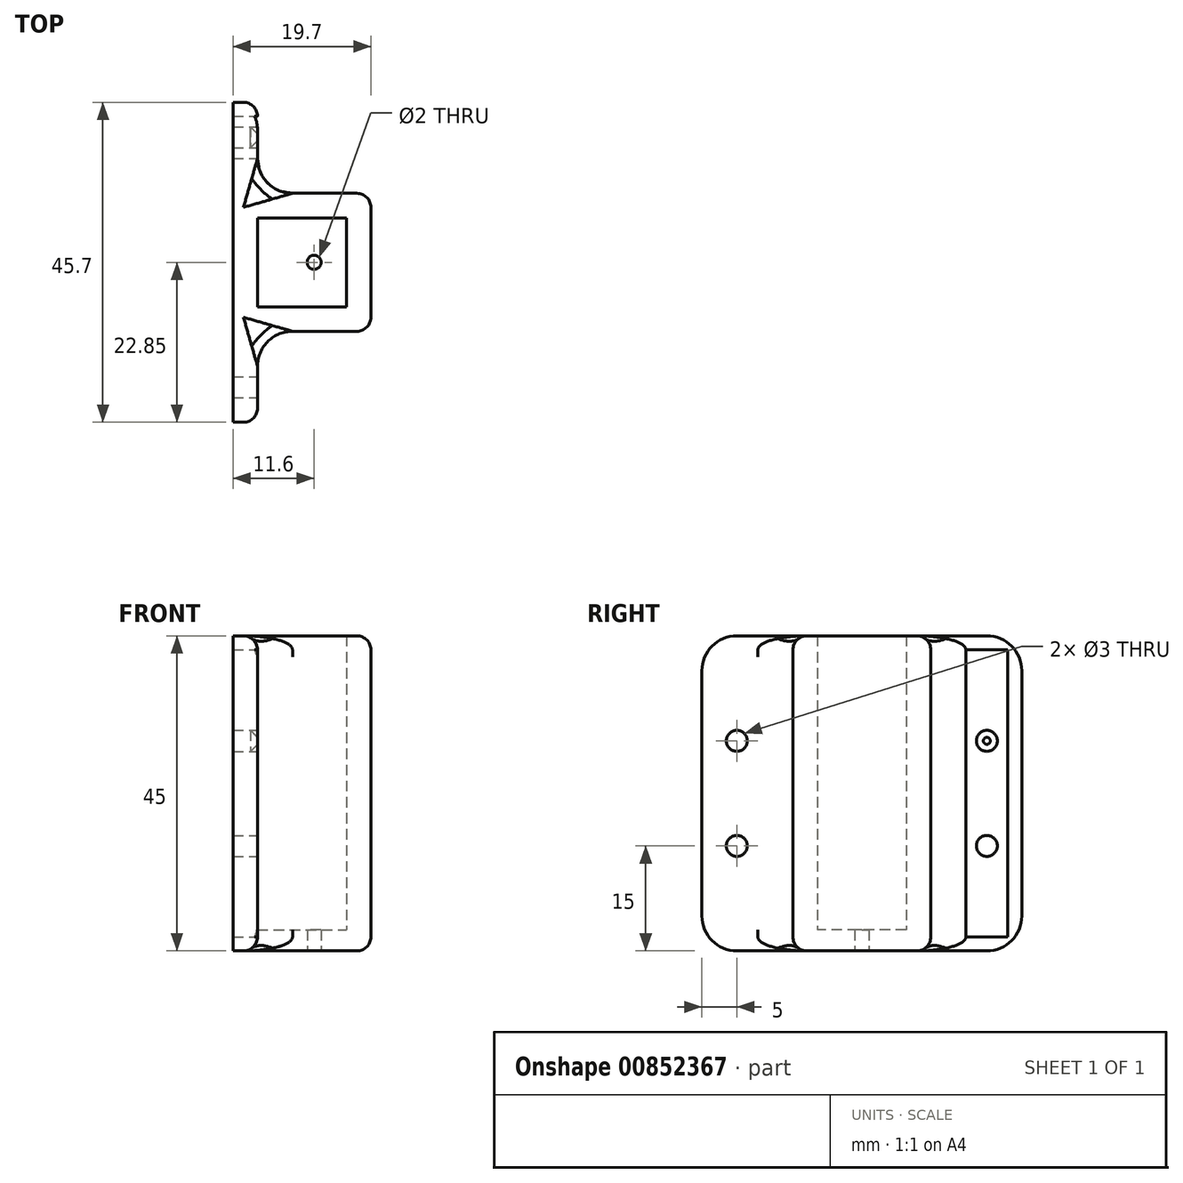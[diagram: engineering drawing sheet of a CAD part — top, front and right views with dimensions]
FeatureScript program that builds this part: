
annotation { "Feature Type Name" : "Feature", "Feature Type Description" : "" }
export const myFeature = defineFeature(function(context is Context, id is Id, definition is map)
    precondition{}
    {
        {
            var Q0;
            Q0=qCreatedBy(makeId("Top.planeOp"),FACE);
            var sketch = newSketch(context, id + "F0", { "sketchPlane" : qUnion([Q0])});
            skLineSegment(sketch, "E0.bottom", {"start": v(0, 6.35) * mm, "end": v(12.7, 6.35) * mm});
            skLineSegment(sketch, "E0.top", {"start": v(0, -6.35) * mm, "end": v(12.7, -6.35) * mm});
            skLineSegment(sketch, "E0.left", {"start": v(0, 6.35) * mm, "end": v(0, -6.35) * mm});
            skLineSegment(sketch, "E0.right", {"start": v(12.7, 6.35) * mm, "end": v(12.7, -6.35) * mm});
            skLineSegment(sketch, "E1.0", {"start": v(0, 9.85) * mm, "end": v(16.2, 9.85) * mm});
            skLineSegment(sketch, "E1.1", {"start": v(-3.5, 9.85) * mm, "end": v(-3.5, -9.85) * mm});
            skLineSegment(sketch, "E1.2", {"start": v(0, -9.85) * mm, "end": v(16.2, -9.85) * mm});
            skLineSegment(sketch, "E1.3", {"start": v(16.2, 9.85) * mm, "end": v(16.2, -9.85) * mm});
            skLineSegment(sketch, "E2.top", {"start": v(-3.5, 22.85) * mm, "end": v(0, 22.85) * mm});
            skLineSegment(sketch, "E2.left", {"start": v(-3.5, -9.85) * mm, "end": v(-3.5, 22.85) * mm});
            skLineSegment(sketch, "E3.trimOffspring", {"start": v(0, -6.35) * mm, "end": v(0, 6.35) * mm});
            skPoint(sketch, "E2.bottom.start.orphan", {"position": v(-3.5, -21.69) * mm});
            skLineSegment(sketch, "E4.trimOffspring", {"start": v(0, 9.85) * mm, "end": v(0, 22.85) * mm});
            skLineSegment(sketch, "E5.MirrorCS", {"start": v(0, -9.85) * mm, "end": v(0, -22.85) * mm});
            skLineSegment(sketch, "E6.MirrorCS", {"start": v(-3.5, -22.85) * mm, "end": v(0, -22.85) * mm});
            skLineSegment(sketch, "E7.MirrorCS", {"start": v(-3.5, 9.85) * mm, "end": v(-3.5, -22.85) * mm});
            skSolve(sketch);
        }
        {
            var Q0;
            Q0=qSketchRegion(id+"F0",true);
            extrude(context, id + "F1", {"entities" : qUnion([Q0]), "depth" : 45 * mm, "offsetDistance" : 25 * mm});
        }
        {
            var Q0;
            Q0=makeQuery(id+"F0.imprint","IMPRINT",FACE,{"disambiguationData":[TD([[makeQuery(id+"F0.imprint","IMPRINT",EDGE,{"derivedFrom":sQuery(id+"F0.wireOp",EDGE,"E0.bottom")}),-1.0]])]});
            extrude(context, id + "F2", {"entities" : qUnion([Q0]), "operationType" : NewBodyOperationType.ADD, "depth" : 3 * mm, "offsetDistance" : 25 * mm});
        }
        {
            var Q0;
            {var subQ0=sQuery(id+"F0.wireOp",EDGE,"E3.trimOffspring");var subQ1=sQuery(id+"F0.wireOp",EDGE,"E0.right");var subQ2=sQuery(id+"F0.wireOp",EDGE,"E0.top");var subQ3=sQuery(id+"F0.wireOp",EDGE,"E0.bottom");Q0=makeQuery(id+"F2.boolean.opBoolean","MERGE",FACE,{"derivedFrom":[makeQuery(id+"F1.opExtrude","CAP_FACE",FACE,{"disambiguationData":[OSD([subQ3,subQ2,subQ1,sQuery(id+"F0.wireOp",EDGE,"E1.0"),sQuery(id+"F0.wireOp",EDGE,"E1.2"),sQuery(id+"F0.wireOp",EDGE,"E1.3"),sQuery(id+"F0.wireOp",EDGE,"E2.top"),sQuery(id+"F0.wireOp",EDGE,"E2.left"),subQ0,sQuery(id+"F0.wireOp",EDGE,"E4.trimOffspring"),sQuery(id+"F0.wireOp",EDGE,"E5.MirrorCS"),sQuery(id+"F0.wireOp",EDGE,"E6.MirrorCS"),sQuery(id+"F0.wireOp",EDGE,"E7.MirrorCS")])],"isStart":true}),makeQuery(id+"F2.opExtrude","CAP_FACE",FACE,{"disambiguationData":[OSD([subQ3,subQ2,subQ1,subQ0])],"isStart":true})]});}
            var sketch = newSketch(context, id + "F3", { "sketchPlane" : qUnion([Q0])});
            skLineSegment(sketch, "E8", {"start": v(0, 0) * mm, "end": v(16.2, 0) * mm, "construction": true});
            skCircle(sketch, "E9", {"center": v(8.1, 0) * mm, "radius": 1 * mm});
            skSolve(sketch);
        }
        {
            var Q0;
            Q0=makeQuery(id+"F3.imprint","IMPRINT",FACE,{"disambiguationData":[TD([[makeQuery(id+"F3.imprint","IMPRINT",EDGE,{"derivedFrom":sQuery(id+"F3.wireOp",EDGE,"E9")}),1.0]])]});
            extrude(context, id + "F4", {"entities" : qUnion([Q0]), "operationType" : NewBodyOperationType.REMOVE, "endBound" : BoundingType.THROUGH_ALL, "oppositeDirection" : true, "depth" : 25 * mm, "offsetDistance" : 25 * mm});
        }
        {
            var Q0;
            Q0=makeQuery(id+"F1.opExtrude","CAP_EDGE",EDGE,{"disambiguationData":[OSD([sQuery(id+"F0.wireOp",EDGE,"E6.MirrorCS")])],"isStart":false});
            var Q1;
            Q1=makeQuery(id+"F1.opExtrude","CAP_EDGE",EDGE,{"disambiguationData":[OSD([sQuery(id+"F0.wireOp",EDGE,"E2.top")])],"isStart":false});
            var Q2;
            Q2=makeQuery(id+"F1.opExtrude","CAP_EDGE",EDGE,{"disambiguationData":[OSD([sQuery(id+"F0.wireOp",EDGE,"E6.MirrorCS")])],"isStart":true});
            var Q3;
            Q3=makeQuery(id+"F1.opExtrude","CAP_EDGE",EDGE,{"disambiguationData":[OSD([sQuery(id+"F0.wireOp",EDGE,"E2.top")])],"isStart":true});
            fillet(context, id + "F5", {"entities" : qUnion([Q0, Q1, Q2, Q3]), "radius" : 5 * mm, "tangentPropagation" : true, "allowEdgeOverflow" : false});
        }
        {
            var Q0;
            Q0=makeQuery(id+"F1.opExtrude","CAP_EDGE",EDGE,{"disambiguationData":[OSD([sQuery(id+"F0.wireOp",EDGE,"E1.3")])],"isStart":false});
            var Q1;
            Q1=makeQuery(id+"F1.opExtrude","CAP_EDGE",EDGE,{"disambiguationData":[OSD([sQuery(id+"F0.wireOp",EDGE,"E1.2")])],"isStart":false});
            var Q2;
            Q2=makeQuery(id+"F1.opExtrude","CAP_EDGE",EDGE,{"disambiguationData":[OSD([sQuery(id+"F0.wireOp",EDGE,"E1.0")])],"isStart":false});
            var Q3;
            Q3=makeQuery(id+"F1.opExtrude","CAP_EDGE",EDGE,{"disambiguationData":[OSD([sQuery(id+"F0.wireOp",EDGE,"E4.trimOffspring")])],"isStart":false});
            var Q4;
            Q4=makeQuery(id+"F1.opExtrude","CAP_EDGE",EDGE,{"disambiguationData":[OSD([sQuery(id+"F0.wireOp",EDGE,"E5.MirrorCS")])],"isStart":false});
            var Q5;
            Q5=makeQuery(id+"F1.opExtrude","SWEPT_EDGE",EDGE,{"disambiguationData":[OSD([sQuery(id+"F0.wireOp",EDGE,"E5.MirrorCS"),sQuery(id+"F0.wireOp",EDGE,"E6.MirrorCS")])]});
            var Q6;
            Q6=makeQuery(id+"F1.opExtrude","SWEPT_EDGE",EDGE,{"disambiguationData":[OSD([sQuery(id+"F0.wireOp",EDGE,"E2.top"),sQuery(id+"F0.wireOp",EDGE,"E4.trimOffspring")])]});
            var Q7;
            Q7=makeQuery(id+"F1.opExtrude","SWEPT_EDGE",EDGE,{"disambiguationData":[OSD([sQuery(id+"F0.wireOp",EDGE,"E1.2"),sQuery(id+"F0.wireOp",EDGE,"E1.3")])]});
            var Q8;
            Q8=makeQuery(id+"F1.opExtrude","SWEPT_EDGE",EDGE,{"disambiguationData":[OSD([sQuery(id+"F0.wireOp",EDGE,"E1.0"),sQuery(id+"F0.wireOp",EDGE,"E1.3")])]});
            var Q9;
            Q9=makeQuery(id+"F1.opExtrude","CAP_EDGE",EDGE,{"disambiguationData":[OSD([sQuery(id+"F0.wireOp",EDGE,"E1.3")])],"isStart":true});
            var Q10;
            Q10=makeQuery(id+"F1.opExtrude","CAP_EDGE",EDGE,{"disambiguationData":[OSD([sQuery(id+"F0.wireOp",EDGE,"E1.2")])],"isStart":true});
            var Q11;
            Q11=makeQuery(id+"F1.opExtrude","CAP_EDGE",EDGE,{"disambiguationData":[OSD([sQuery(id+"F0.wireOp",EDGE,"E1.0")])],"isStart":true});
            var Q12;
            Q12=makeQuery(id+"F1.opExtrude","CAP_EDGE",EDGE,{"disambiguationData":[OSD([sQuery(id+"F0.wireOp",EDGE,"E5.MirrorCS")])],"isStart":true});
            var Q13;
            Q13=makeQuery(id+"F1.opExtrude","CAP_EDGE",EDGE,{"disambiguationData":[OSD([sQuery(id+"F0.wireOp",EDGE,"E4.trimOffspring")])],"isStart":true});
            fillet(context, id + "F6", {"entities" : qUnion([Q0, Q1, Q2, Q3, Q4, Q5, Q6, Q7, Q8, Q9, Q10, Q11, Q12, Q13]), "radius" : 2 * mm, "tangentPropagation" : true, "allowEdgeOverflow" : false});
        }
        {
            var Q0;
            Q0=makeQuery(id+"F1.opExtrude","SWEPT_EDGE",EDGE,{"disambiguationData":[OSD([sQuery(id+"F0.wireOp",EDGE,"E1.2"),sQuery(id+"F0.wireOp",EDGE,"E5.MirrorCS")])]});
            var Q1;
            Q1=makeQuery(id+"F1.opExtrude","SWEPT_EDGE",EDGE,{"disambiguationData":[OSD([sQuery(id+"F0.wireOp",EDGE,"E1.0"),sQuery(id+"F0.wireOp",EDGE,"E4.trimOffspring")])]});
            fillet(context, id + "F7", {"entities" : qUnion([Q0, Q1]), "radius" : 5 * mm, "tangentPropagation" : true, "allowEdgeOverflow" : false});
        }
        {
            var Q0;
            Q0=makeQuery(id+"F1.opExtrude","SWEPT_FACE",FACE,{"disambiguationData":[OSD([sQuery(id+"F0.wireOp",EDGE,"E5.MirrorCS")])]});
            var sketch = newSketch(context, id + "F8", { "sketchPlane" : qUnion([Q0])});
            skLineSegment(sketch, "E10.0.0", {"start": v(-20.85, 2) * mm, "end": v(-14.85, 2) * mm});
            skLineSegment(sketch, "E10.0.1", {"start": v(-14.85, 2) * mm, "end": v(-14.85, 43) * mm});
            skLineSegment(sketch, "E10.0.2", {"start": v(-14.85, 43) * mm, "end": v(-20.85, 43) * mm});
            skLineSegment(sketch, "E10.0.3", {"start": v(-20.85, 43) * mm, "end": v(-20.85, 2) * mm});
            skLineSegment(sketch, "E11.0.0", {"start": v(20.85, 43) * mm, "end": v(14.85, 43) * mm});
            skLineSegment(sketch, "E11.0.1", {"start": v(14.85, 43) * mm, "end": v(14.85, 2) * mm});
            skLineSegment(sketch, "E11.0.2", {"start": v(14.85, 2) * mm, "end": v(20.85, 2) * mm});
            skLineSegment(sketch, "E11.0.3", {"start": v(20.85, 2) * mm, "end": v(20.85, 43) * mm});
            skLineSegment(sketch, "E12", {"start": v(-17.85, 43) * mm, "end": v(-17.85, 2) * mm, "construction": true});
            skCircle(sketch, "E13", {"center": v(-17.85, 30) * mm, "radius": 1.5 * mm});
            skCircle(sketch, "E14", {"center": v(-17.85, 15) * mm, "radius": 1.5 * mm});
            skLineSegment(sketch, "E15", {"start": v(0, 0) * mm, "end": v(0, 47.04) * mm, "construction": true});
            skCircle(sketch, "E16.MirrorC", {"center": v(17.85, 30) * mm, "radius": 1.5 * mm});
            skCircle(sketch, "E17.MirrorC", {"center": v(17.85, 15) * mm, "radius": 1.5 * mm});
            skSolve(sketch);
        }
        {
            var Q0;
            Q0=makeQuery(id+"F8.imprint","IMPRINT",FACE,{"disambiguationData":[TD([[makeQuery(id+"F8.imprint","IMPRINT",EDGE,{"derivedFrom":sQuery(id+"F8.wireOp",EDGE,"E13")}),1.0]])]});
            var Q1;
            Q1=makeQuery(id+"F8.imprint","IMPRINT",FACE,{"disambiguationData":[TD([[makeQuery(id+"F8.imprint","IMPRINT",EDGE,{"derivedFrom":sQuery(id+"F8.wireOp",EDGE,"E14")}),1.0]])]});
            var Q2;
            Q2=makeQuery(id+"F8.imprint","IMPRINT",FACE,{"disambiguationData":[TD([[makeQuery(id+"F8.imprint","IMPRINT",EDGE,{"derivedFrom":sQuery(id+"F8.wireOp",EDGE,"E17.MirrorC")}),-1.0]])]});
            var Q3;
            Q3=makeQuery(id+"F8.imprint","IMPRINT",FACE,{"disambiguationData":[TD([[makeQuery(id+"F8.imprint","IMPRINT",EDGE,{"derivedFrom":sQuery(id+"F8.wireOp",EDGE,"E16.MirrorC")}),-1.0]])]});
            extrude(context, id + "F9", {"entities" : qUnion([Q0, Q1, Q2, Q3]), "operationType" : NewBodyOperationType.REMOVE, "endBound" : BoundingType.THROUGH_ALL, "oppositeDirection" : true, "depth" : 25 * mm, "offsetDistance" : 25 * mm});
        }
        {
            var Q0;
            Q0=makeQuery(id+"F9.boolean.opBoolean","COPY",EDGE,{"derivedFrom":makeQuery(id+"F9.opExtrude","CAP_EDGE",EDGE,{"disambiguationData":[OSD([sQuery(id+"F8.wireOp",EDGE,"E13")])],"isStart":true})});
            var Q1;
            Q1=makeQuery(id+"F9.boolean.opBoolean","COPY",EDGE,{"derivedFrom":makeQuery(id+"F9.opExtrude","CAP_EDGE",EDGE,{"disambiguationData":[OSD([sQuery(id+"F8.wireOp",EDGE,"E14")])],"isStart":true})});
            var Q2;
            Q2=makeQuery(id+"F9.boolean.opBoolean","COPY",EDGE,{"derivedFrom":makeQuery(id+"F9.opExtrude","CAP_EDGE",EDGE,{"disambiguationData":[OSD([sQuery(id+"F8.wireOp",EDGE,"E17.MirrorC")])],"isStart":true})});
            var Q3;
            Q3=makeQuery(id+"F9.boolean.opBoolean","COPY",EDGE,{"derivedFrom":makeQuery(id+"F9.opExtrude","CAP_EDGE",EDGE,{"disambiguationData":[OSD([sQuery(id+"F8.wireOp",EDGE,"E16.MirrorC")])],"isStart":true})});
            chamfer(context, id + "F10", {"entities" : qUnion([Q0, Q1, Q2, Q3]), "width" : 1 * mm, "tangentPropagation" : true});
        }
    });
